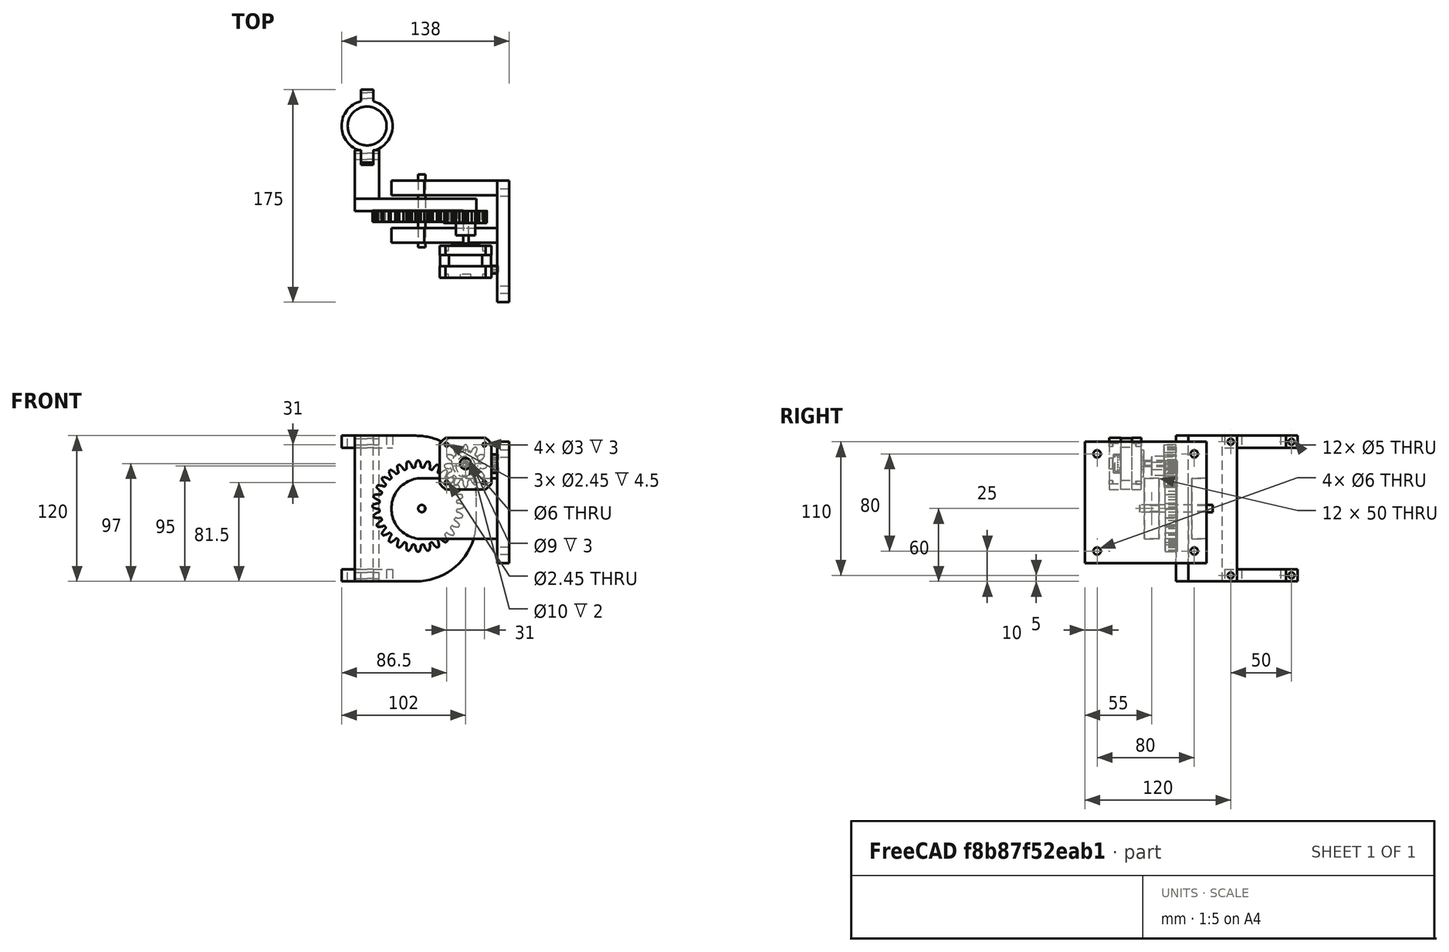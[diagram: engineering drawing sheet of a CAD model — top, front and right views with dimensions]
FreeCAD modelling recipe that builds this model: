
FCSTD DOCUMENT  (FreeCAD 0.18R4 (GitTag))
Label: RotorZ
License: All rights reserved
LicenseURL: http://en.wikipedia.org/wiki/All_rights_reserved
objects: Part::Cylinder×31, Part::Cut×22, Part::Box×14, Part::MultiFuse×13, Part::Fuse×4, Part::Fillet×2, Part::Part2DObjectPython×1, Part::Extrusion×1
note: 88 computed .brp shape members not serialized (recipe doc carries the construction recipe); baked Part::Feature solids carry a one-line shape summary decoded from their .brp

FEATURE [Part::Box] Box  label="Cubo"
  AttacherType = Attacher::AttachEngine3D
  Height = 10
  Length = 10
  Placement = pos=(-5,-30,0) rot=(0,0,1;0rad)
  Width = 60
FEATURE [Part::Box] Box001  label="Cubo001"
  AttacherType = Attacher::AttachEngine3D
  Height = 10
  Length = 21
  Placement = pos=(0,-30,0) rot=(0,0,1;0rad)
  Width = 60
FEATURE [Part::Cylinder] Cylinder  label="Cilindro"
  Angle = 360
  AttacherType = Attacher::AttachEngine3D
  Height = 10
  Placement = pos=(-5,-25,5) rot=(0,1,0;1.5708rad)
  Radius = 2.5
FEATURE [Part::Cylinder] Cylinder003  label="Cilindro001"
  Angle = 360
  AttacherType = Attacher::AttachEngine3D
  Height = 10
  Placement = pos=(-5,25,5) rot=(0,1,0;1.5708rad)
  Radius = 2.5
FEATURE [Part::MultiFuse] Fusion001  label="Agug"
  Shapes = -> [Cylinder,Cylinder003]
FEATURE [Part::Box] Box012  label="Cubo012"
  AttacherType = Attacher::AttachEngine3D
  Height = 120
  Length = 10
  Placement = pos=(-5,-72,0) rot=(0,0,1;0rad)
  Width = 12
FEATURE [Part::Box] Box013  label="Cubo013"
  AttacherType = Attacher::AttachEngine3D
  Height = 120
  Length = 20
  Placement = pos=(-10,-100,0) rot=(0,0,1;0rad)
  Width = 40
FEATURE [Part::Box] Box014  label="Cubo014"
  AttacherType = Attacher::AttachEngine3D
  Height = 120
  Length = 100
  Placement = pos=(-10,-46,0) rot=(0,0,1;0rad)
  Width = 10
FEATURE [Part::Part2DObjectPython] InvoluteGear  # Draft 2D object (typed FeaturePython)
  ExternalGear = true
  HighPrecision = true
  Modules = 2.5
  NumberOfTeeth = 28
  PressureAngle = 20
FEATURE [Part::Extrusion] Extrude
  Base = -> InvoluteGear
  Dir = (0,0,1)
  DirMode = 2
  FaceMakerClass = Part::FaceMakerBullseye
  LengthFwd = 10
  LengthRev = 0
  Placement = pos=(42,-45,62) rot=(1,0,0;1.5708rad)
  Solid = true
  Symmetric = false
FEATURE [Part::Box] Box015  label="Cubo015"
  AttacherType = Attacher::AttachEngine3D
  Height = 12
  Length = 70
  Placement = pos=(31,-70,-13) rot=(0,0,1;0rad)
  Width = 50
FEATURE [Part::Cylinder] Cylinder016  label="Cilindro008"
  Angle = 360
  AttacherType = Attacher::AttachEngine3D
  Height = 12
  Placement = pos=(29,-45,-13) rot=(0,0,1;0rad)
  Radius = 25
FEATURE [Part::Cylinder] Cylinder017  label="Cilindro009"
  Angle = 360
  AttacherType = Attacher::AttachEngine3D
  Height = 12
  Placement = pos=(29,-45,-13) rot=(0,0,1;0rad)
  Radius = 3
FEATURE [Part::Cut] Cut017
  Base = -> Cylinder016
  Tool = -> Cylinder017
FEATURE [Part::MultiFuse] Fusion008  label="lateral"
  Placement = pos=(16,-34,105) rot=(1,0,0;1.5708rad)
  Shapes = -> [Box015,Cut017]
FEATURE [Part::Box] Box016  label="Cubo016"
  AttacherType = Attacher::AttachEngine3D
  Height = 12
  Length = 70
  Placement = pos=(31,-70,-13) rot=(0,0,1;0rad)
  Width = 50
FEATURE [Part::Cylinder] Cylinder018  label="Cilindro010"
  Angle = 360
  AttacherType = Attacher::AttachEngine3D
  Height = 12
  Placement = pos=(29,-45,-13) rot=(0,0,1;0rad)
  Radius = 25
FEATURE [Part::Cylinder] Cylinder019  label="Cilindro011"
  Angle = 360
  AttacherType = Attacher::AttachEngine3D
  Height = 12
  Placement = pos=(29,-45,-13) rot=(0,0,1;0rad)
  Radius = 3
FEATURE [Part::Cut] Cut018
  Base = -> Cylinder018
  Tool = -> Cylinder019
FEATURE [Part::MultiFuse] Fusion009  label="lateral001"
  Placement = pos=(16,-73,105) rot=(1,0,0;1.5708rad)
  Shapes = -> [Box016,Cut018]
FEATURE [Part::Box] Box017  label="BaseEjeZ"
  AttacherType = Attacher::AttachEngine3D
  Height = 100
  Length = 10
  Placement = pos=(107,-121,15) rot=(0,0,1;0rad)
  Width = 100
FEATURE [Part::Cylinder] Cylinder020  label="Cilindro012"
  Angle = 360
  AttacherType = Attacher::AttachEngine3D
  Height = 60
  Placement = pos=(45,-16,60) rot=(1,0,0;1.5708rad)
  Radius = 3
FEATURE [Part::Fillet] Fillet
  Base = -> Box014
  Edges = 1 edges r=50: [Edge8]
FEATURE [Part::Fillet] Fillet001
  Base = -> Fillet
  Edges = 1 edges r=50: [Edge3]
FEATURE [Part::Cylinder] Cylinder021  label="Cilindro 32"
  Angle = 360
  AttacherType = Attacher::AttachEngine3D
  Height = 10
  Radius = 16
FEATURE [Part::Cylinder] Cylinder022  label="Cilindro42"
  Angle = 360
  AttacherType = Attacher::AttachEngine3D
  Height = 10
  Radius = 21
FEATURE [Part::Cut] Cut019
  Base = -> Cylinder022
  Tool = -> Cylinder021
FEATURE [Part::Fuse] Fusion
  Base = -> Box
  Tool = -> Cut019
FEATURE [Part::Cut] Cut
  Base = -> Fusion
  Tool = -> Fusion001
FEATURE [Part::Cut] Cut020
  Base = -> Cut
  Tool = -> Box001
FEATURE [Part::Cylinder] Cylinder023  label="Cilindro013"
  Angle = 360
  AttacherType = Attacher::AttachEngine3D
  Height = 10
  Radius = 16
FEATURE [Part::Cut] Cut021  label="Brida"
  Base = -> Cut020
  Placement = pos=(0,4,10) rot=(0,1,0;3.14159rad)
  Tool = -> Cylinder023
FEATURE [Part::Cylinder] Cylinder024  label="Cilindro014"
  Angle = 360
  AttacherType = Attacher::AttachEngine3D
  Height = 10
  Placement = pos=(-5,25,5) rot=(0,1,0;1.5708rad)
  Radius = 2.5
FEATURE [Part::Box] Box018  label="Cubo018"
  AttacherType = Attacher::AttachEngine3D
  Height = 10
  Length = 10
  Placement = pos=(-5,-30,0) rot=(0,0,1;0rad)
  Width = 60
FEATURE [Part::Cylinder] Cylinder025  label="Cilindro015"
  Angle = 360
  AttacherType = Attacher::AttachEngine3D
  Height = 10
  Placement = pos=(-5,-25,5) rot=(0,1,0;1.5708rad)
  Radius = 2.5
FEATURE [Part::Box] Box019  label="Cubo019"
  AttacherType = Attacher::AttachEngine3D
  Height = 10
  Length = 21
  Placement = pos=(0,-30,0) rot=(0,0,1;0rad)
  Width = 60
FEATURE [Part::MultiFuse] Fusion010  label="Agug001"
  Shapes = -> [Cylinder025,Cylinder024]
FEATURE [Part::Cylinder] Cylinder026  label="Cilindro 033"
  Angle = 360
  AttacherType = Attacher::AttachEngine3D
  Height = 10
  Radius = 16
FEATURE [Part::Cylinder] Cylinder027  label="Cilindro016"
  Angle = 360
  AttacherType = Attacher::AttachEngine3D
  Height = 10
  Radius = 21
FEATURE [Part::Cut] Cut024
  Base = -> Cylinder027
  Tool = -> Cylinder026
FEATURE [Part::Fuse] Fusion011
  Base = -> Box018
  Tool = -> Cut024
FEATURE [Part::Cut] Cut025
  Base = -> Fusion011
  Tool = -> Fusion010
FEATURE [Part::Cut] Cut022
  Base = -> Cut025
  Tool = -> Box019
FEATURE [Part::Cylinder] Cylinder028  label="Cilindro017"
  Angle = 360
  AttacherType = Attacher::AttachEngine3D
  Height = 10
  Radius = 16
FEATURE [Part::Cut] Cut023  label="Brida001"
  Base = -> Cut022
  Placement = pos=(0,4,0) rot=(0,0,1;0rad)
  Tool = -> Cylinder028
FEATURE [Part::Cylinder] Cylinder029  label="Cilindro018"
  Angle = 360
  AttacherType = Attacher::AttachEngine3D
  Height = 10
  Placement = pos=(-5,25,5) rot=(0,1,0;1.5708rad)
  Radius = 2.5
FEATURE [Part::Box] Box020  label="Cubo020"
  AttacherType = Attacher::AttachEngine3D
  Height = 10
  Length = 10
  Placement = pos=(-5,-30,0) rot=(0,0,1;0rad)
  Width = 60
FEATURE [Part::Cylinder] Cylinder030  label="Cilindro019"
  Angle = 360
  AttacherType = Attacher::AttachEngine3D
  Height = 10
  Placement = pos=(-5,-25,5) rot=(0,1,0;1.5708rad)
  Radius = 2.5
FEATURE [Part::Box] Box021  label="Cubo021"
  AttacherType = Attacher::AttachEngine3D
  Height = 10
  Length = 21
  Placement = pos=(0,-30,0) rot=(0,0,1;0rad)
  Width = 60
FEATURE [Part::MultiFuse] Fusion012  label="Agug002"
  Shapes = -> [Cylinder030,Cylinder029]
FEATURE [Part::Cylinder] Cylinder031  label="Cilindro 034"
  Angle = 360
  AttacherType = Attacher::AttachEngine3D
  Height = 10
  Radius = 16
FEATURE [Part::Cylinder] Cylinder032  label="Cilindro020"
  Angle = 360
  AttacherType = Attacher::AttachEngine3D
  Height = 10
  Radius = 21
FEATURE [Part::Cut] Cut028
  Base = -> Cylinder032
  Tool = -> Cylinder031
FEATURE [Part::Fuse] Fusion013
  Base = -> Box020
  Tool = -> Cut028
FEATURE [Part::Cut] Cut029
  Base = -> Fusion013
  Tool = -> Fusion012
FEATURE [Part::Cut] Cut026
  Base = -> Cut029
  Tool = -> Box021
FEATURE [Part::Cylinder] Cylinder033  label="Cilindro021"
  Angle = 360
  AttacherType = Attacher::AttachEngine3D
  Height = 10
  Radius = 16
FEATURE [Part::Cut] Cut027  label="Brida002"
  Base = -> Cut026
  Placement = pos=(0,4,120) rot=(0,1,0;3.14159rad)
  Tool = -> Cylinder033
FEATURE [Part::Cylinder] Cylinder034  label="Cilindro022"
  Angle = 360
  AttacherType = Attacher::AttachEngine3D
  Height = 10
  Radius = 21
FEATURE [Part::Cylinder] Cylinder035  label="Cilindro023"
  Angle = 360
  AttacherType = Attacher::AttachEngine3D
  Height = 10
  Placement = pos=(-5,25,5) rot=(0,1,0;1.5708rad)
  Radius = 2.5
FEATURE [Part::Cylinder] Cylinder036  label="Cilindro024"
  Angle = 360
  AttacherType = Attacher::AttachEngine3D
  Height = 10
  Placement = pos=(-5,-25,5) rot=(0,1,0;1.5708rad)
  Radius = 2.5
FEATURE [Part::MultiFuse] Fusion014  label="Agug003"
  Shapes = -> [Cylinder036,Cylinder035]
FEATURE [Part::Box] Box022  label="Cubo022"
  AttacherType = Attacher::AttachEngine3D
  Height = 10
  Length = 10
  Placement = pos=(-5,-30,0) rot=(0,0,1;0rad)
  Width = 60
FEATURE [Part::Cylinder] Cylinder037  label="Cilindro 035"
  Angle = 360
  AttacherType = Attacher::AttachEngine3D
  Height = 10
  Radius = 16
FEATURE [Part::Cut] Cut033
  Base = -> Cylinder034
  Tool = -> Cylinder037
FEATURE [Part::Fuse] Fusion015
  Base = -> Box022
  Tool = -> Cut033
FEATURE [Part::Cut] Cut032
  Base = -> Fusion015
  Tool = -> Fusion014
FEATURE [Part::Box] Box023  label="Cubo023"
  AttacherType = Attacher::AttachEngine3D
  Height = 10
  Length = 21
  Placement = pos=(0,-30,0) rot=(0,0,1;0rad)
  Width = 60
FEATURE [Part::Cut] Cut030
  Base = -> Cut032
  Tool = -> Box023
FEATURE [Part::Cylinder] Cylinder038  label="Cilindro025"
  Angle = 360
  AttacherType = Attacher::AttachEngine3D
  Height = 10
  Radius = 16
FEATURE [Part::Cut] Cut031  label="Brida003"
  Base = -> Cut030
  Placement = pos=(0,4,110) rot=(0,0,1;0rad)
  Tool = -> Cylinder038
FEATURE [Part::Cut] Cut035  label="Engranaje"
  Base = -> Fusion
  Placement = pos=(31,-46,99) rot=(1,0,0;1.5708rad)
FEATURE [Part::MultiFuse] Fusion016  label="Motor"
  Placement = pos=(81,-101,97) rot=(-1,0,0;1.5708rad)
  Shapes = -> [Fusion]
FEATURE [Part::MultiFuse] Fusion017  label="Brida1"
  Shapes = -> [Cut021,Cut023]
FEATURE [Part::MultiFuse] Fusion018  label="Brida2"
  Shapes = -> [Cut027,Cut031]
FEATURE [Part::MultiFuse] Fusion019  label="Bridas"
  Placement = pos=(0,20,0) rot=(0,0,1;0rad)
  Shapes = -> [Fusion017,Fusion018]
FEATURE [Part::MultiFuse] Fusion020  label="Udesoporte"
  Shapes = -> [Fusion008,Fusion009,Box017]
FEATURE [Part::Cut] Cut036  label="UdeBridas"
  Base = -> Box013
  Placement = pos=(0,64,0) rot=(0,0,1;0rad)
  Tool = -> Box012
FEATURE [Part::Cylinder] Cylinder039  label="Cilindro026"
  Angle = 360
  AttacherType = Attacher::AttachEngine3D
  Height = 20
  Placement = pos=(-10,59,5) rot=(0,1,0;1.5708rad)
  Radius = 2.5
FEATURE [Part::Cylinder] Cylinder040  label="Cilindro027"
  Angle = 360
  AttacherType = Attacher::AttachEngine3D
  Height = 20
  Placement = pos=(-10,59,115) rot=(0,1,0;1.5708rad)
  Radius = 2.5
FEATURE [Part::MultiFuse] Fusion021  label="UamareBridas"
  Placement = pos=(0,-60,0) rot=(0,0,1;0rad)
  Shapes = -> [Cylinder039,Cylinder040]
FEATURE [Part::Cut] Cut037
  Base = -> Cut036
  Tool = -> Fusion021
FEATURE [Part::Cylinder] Cylinder041  label="Cilindro028"
  Angle = 360
  AttacherType = Attacher::AttachEngine3D
  Height = 10
  Placement = pos=(117,-31,105) rot=(0,1,0;4.71239rad)
  Radius = 3
FEATURE [Part::Cylinder] Cylinder042  label="Cilindro029"
  Angle = 360
  AttacherType = Attacher::AttachEngine3D
  Height = 10
  Placement = pos=(117,-111,25) rot=(0,-1,0;1.5708rad)
  Radius = 3
FEATURE [Part::Cylinder] Cylinder043  label="Cilindro030"
  Angle = 360
  AttacherType = Attacher::AttachEngine3D
  Height = 10
  Placement = pos=(117,-31,25) rot=(0,-1,0;1.5708rad)
  Radius = 3
FEATURE [Part::Cylinder] Cylinder044  label="Cilindro031"
  Angle = 360
  AttacherType = Attacher::AttachEngine3D
  Height = 10
  Placement = pos=(117,-111,105) rot=(0,-1,0;1.5708rad)
  Radius = 3
FEATURE [Part::MultiFuse] Fusion022  label="Afu tornillos"
  Shapes = -> [Cylinder044,Cylinder043,Cylinder042,Cylinder041]
FEATURE [Part::Cut] Cut038
  Base = -> Fusion020
  Tool = -> Fusion022
